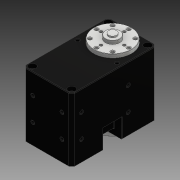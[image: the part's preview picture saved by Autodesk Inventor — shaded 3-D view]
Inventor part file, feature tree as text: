
AUTODESK INVENTOR PART (.ipt)
format: ipt  version: 2016 (Build 200138000, 138)  size: 419,840 bytes
history: native  units: mm
features: other x3, extrude x1, sketch x1, imported_body x1
ambient origin geometry x8: Origin, YZ Plane, XZ Plane, XY Plane, X Axis, Y Axis, Z Axis, Center Point
bodies: Body1 (feature_tree)
feature tree (6):
  other  "<userpath>\Dropbox\Snake\SnakeRobot_ver2\cad\parameter_base.xlsx"
  other  "ソリッド1"
  other  "作業平面1"
  extrude  "押し出し1"  Depth=1.0mm
  sketch  "スケッチ1"
  imported_body  "Base1"
